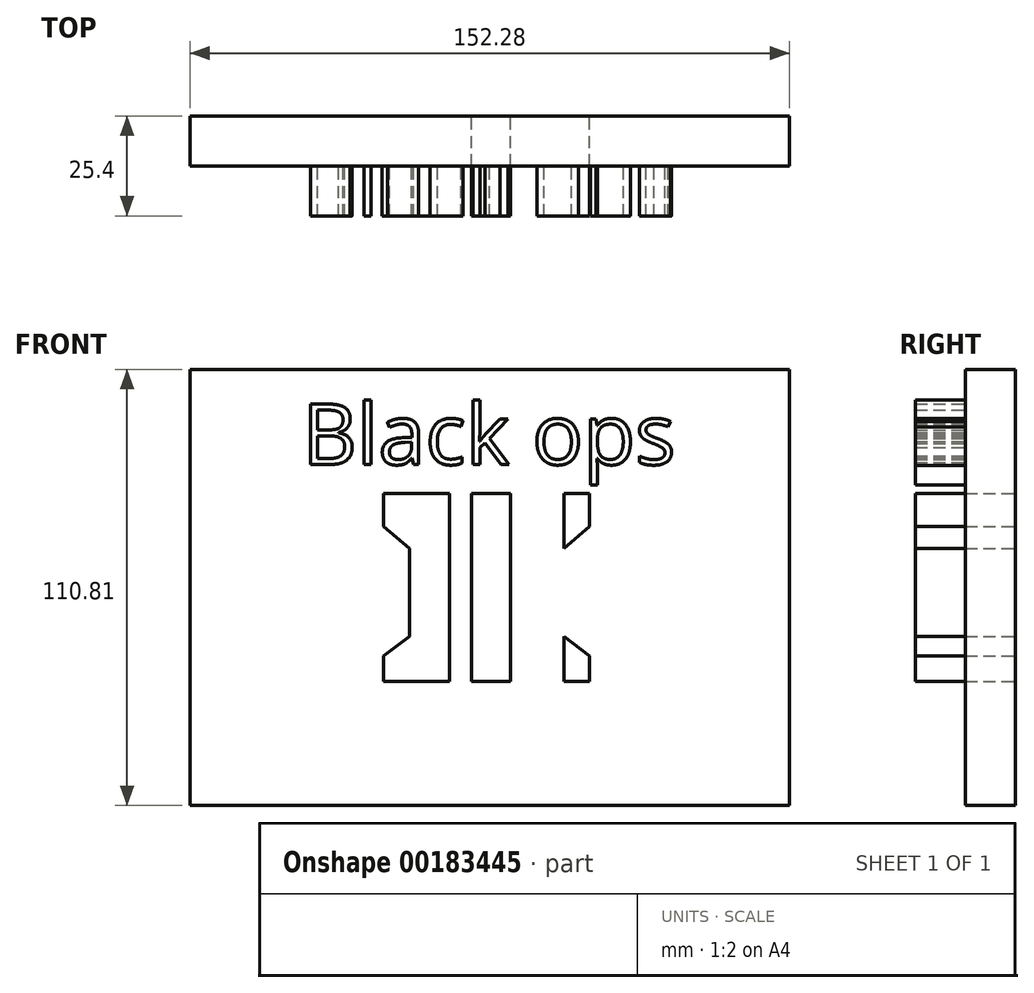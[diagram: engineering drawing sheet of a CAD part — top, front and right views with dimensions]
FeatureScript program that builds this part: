
annotation { "Feature Type Name" : "Feature", "Feature Type Description" : "" }
export const myFeature = defineFeature(function(context is Context, id is Id, definition is map)
    precondition{}
    {
        {
            var Q0;
            Q0=qCreatedBy(makeId("Front.planeOp"),FACE);
            var sketch = newSketch(context, id + "F0", { "sketchPlane" : qUnion([Q0])});
            skLineSegment(sketch, "E0.bottom", {"start": v(-4.33, 24.3) * mm, "end": v(5.57, 24.3) * mm});
            skLineSegment(sketch, "E0.top", {"start": v(-4.33, -23.37) * mm, "end": v(5.57, -23.37) * mm});
            skLineSegment(sketch, "E0.left", {"start": v(-4.33, 24.3) * mm, "end": v(-4.33, -23.37) * mm});
            skLineSegment(sketch, "E0.right", {"start": v(5.57, 24.3) * mm, "end": v(5.57, -23.37) * mm});
            skLineSegment(sketch, "E1.bottom", {"start": v(9.6, 24.3) * mm, "end": v(19.2, 24.3) * mm});
            skLineSegment(sketch, "E1.top", {"start": v(9.6, 24.3) * mm, "end": v(19.2, 24.3) * mm});
            skLineSegment(sketch, "E1.left", {"start": v(9.6, 24.3) * mm, "end": v(9.6, 24.3) * mm});
            skLineSegment(sketch, "E1.right", {"start": v(19.2, 24.3) * mm, "end": v(19.2, 24.3) * mm});
            skLineSegment(sketch, "E2.bottom", {"start": v(19.2, 24.3) * mm, "end": v(10.21, 24.3) * mm});
            skLineSegment(sketch, "E2.top", {"start": v(19.2, -23.37) * mm, "end": v(10.21, -23.37) * mm});
            skLineSegment(sketch, "E2.left", {"start": v(19.2, 24.3) * mm, "end": v(19.2, -23.37) * mm});
            skLineSegment(sketch, "E2.right", {"start": v(10.21, 24.3) * mm, "end": v(10.21, -23.37) * mm});
            skLineSegment(sketch, "E3.bottom", {"start": v(-10.52, 24.3) * mm, "end": v(-20.12, 24.3) * mm});
            skLineSegment(sketch, "E3.top", {"start": v(-10.52, 24.3) * mm, "end": v(-20.12, 24.3) * mm});
            skLineSegment(sketch, "E3.left", {"start": v(-10.52, 24.3) * mm, "end": v(-10.52, 24.3) * mm});
            skLineSegment(sketch, "E3.right", {"start": v(-20.12, 24.3) * mm, "end": v(-20.12, 24.3) * mm});
            skLineSegment(sketch, "E4.bottom", {"start": v(-20.12, 24.3) * mm, "end": v(-9.9, 24.3) * mm});
            skLineSegment(sketch, "E4.top", {"start": v(-20.12, -23.37) * mm, "end": v(-9.9, -23.37) * mm});
            skLineSegment(sketch, "E4.left", {"start": v(-20.12, 24.3) * mm, "end": v(-20.12, -23.37) * mm});
            skLineSegment(sketch, "E4.right", {"start": v(-9.9, 24.3) * mm, "end": v(-9.9, -23.37) * mm});
            skLineSegment(sketch, "E5", {"start": v(-20.12, 24.3) * mm, "end": v(-26.62, 24.3) * mm});
            skLineSegment(sketch, "E6", {"start": v(-26.62, 24.3) * mm, "end": v(-26.62, 15.94) * mm});
            skLineSegment(sketch, "E7", {"start": v(-26.62, 15.94) * mm, "end": v(-20.12, 10.37) * mm});
            skLineSegment(sketch, "E8", {"start": v(-20.12, 10.37) * mm, "end": v(-20.12, -23.37) * mm});
            skLineSegment(sketch, "E9", {"start": v(-20.12, -23.37) * mm, "end": v(-26.62, -23.37) * mm});
            skLineSegment(sketch, "E10", {"start": v(-26.62, -23.37) * mm, "end": v(-26.62, -16.87) * mm});
            skLineSegment(sketch, "E11", {"start": v(-26.62, -16.87) * mm, "end": v(-20.12, -11.92) * mm});
            skLineSegment(sketch, "E12", {"start": v(19.2, 24.3) * mm, "end": v(25.69, 24.3) * mm});
            skLineSegment(sketch, "E13", {"start": v(25.69, 24.3) * mm, "end": v(25.69, 15.94) * mm});
            skLineSegment(sketch, "E14", {"start": v(25.69, 15.94) * mm, "end": v(19.2, 10.37) * mm});
            skLineSegment(sketch, "E15", {"start": v(19.2, -23.37) * mm, "end": v(25.69, -23.37) * mm});
            skLineSegment(sketch, "E16", {"start": v(25.69, -23.37) * mm, "end": v(25.69, -16.87) * mm});
            skLineSegment(sketch, "E17", {"start": v(25.69, -16.87) * mm, "end": v(19.2, -11.92) * mm});
            skSolve(sketch);
        }
        {
            var Q0;
            Q0=qCreatedBy(makeId("Front.planeOp"),FACE);
            var sketch = newSketch(context, id + "F1", { "sketchPlane" : qUnion([Q0])});
            skSolve(sketch);
        }
        {
            var Q0;
            Q0 = qSketchRegion(id + "F1", true);
            var Q1;
            {var subQ0=sQuery(id+"F0.wireOp",EDGE,"E9");Q1=makeQuery(id+"F0.imprint","IMPRINT",FACE,{"disambiguationData":[TD([[makeQuery(id+"F0.imprint","IMPRINT",EDGE,{"derivedFrom":subQ0}),-1.0]])]});}
            var Q2;
            {var subQ4=sQuery(id+"F0.wireOp",EDGE,"E4.top");Q2=makeQuery(id+"F0.imprint","IMPRINT",FACE,{"disambiguationData":[TD([[makeQuery(id+"F0.imprint","IMPRINT",EDGE,{"derivedFrom":subQ4}),1.0]])]});}
            var Q3;
            Q3=makeQuery(id+"F0.imprint","IMPRINT",FACE,{"disambiguationData":[TD([[makeQuery(id+"F0.imprint","IMPRINT",EDGE,{"derivedFrom":sQuery(id+"F0.wireOp",EDGE,"E4.left")}),-1.0]])]});
            var Q4;
            Q4=makeQuery(id+"F0.imprint","IMPRINT",FACE,{"disambiguationData":[TD([[makeQuery(id+"F0.imprint","IMPRINT",EDGE,{"derivedFrom":sQuery(id+"F0.wireOp",EDGE,"E0.bottom")}),-1.0]])]});
            var Q5;
            {var subQ3=sQuery(id+"F0.wireOp",EDGE,"E2.bottom");Q5=makeQuery(id+"F0.imprint","IMPRINT",FACE,{"disambiguationData":[TD([[makeQuery(id+"F0.imprint","IMPRINT",EDGE,{"derivedFrom":subQ3}),1.0]])]});}
            var Q6;
            {var subQ0=sQuery(id+"F0.wireOp",EDGE,"E12");Q6=makeQuery(id+"F0.imprint","IMPRINT",FACE,{"disambiguationData":[TD([[makeQuery(id+"F0.imprint","IMPRINT",EDGE,{"derivedFrom":subQ0}),-1.0]])]});}
            var Q7;
            {var subQ0=sQuery(id+"F0.wireOp",EDGE,"E15");Q7=makeQuery(id+"F0.imprint","IMPRINT",FACE,{"disambiguationData":[TD([[makeQuery(id+"F0.imprint","IMPRINT",EDGE,{"derivedFrom":subQ0}),1.0]])]});}
            extrude(context, id + "F2", {"entities" : qUnion([Q0, Q1, Q2, Q3, Q4, Q5, Q6, Q7]), "depth" : 25.4 * mm});
        }
        {
            var Q0;
            Q0=qCreatedBy(makeId("Front.planeOp"),FACE);
            var sketch = newSketch(context, id + "F3", { "sketchPlane" : qUnion([Q0])});
            skLineSegment(sketch, "E18.bottom", {"start": v(76.45, 55.87) * mm, "end": v(-75.83, 55.87) * mm});
            skLineSegment(sketch, "E18.top", {"start": v(76.45, -54.94) * mm, "end": v(-75.83, -54.94) * mm});
            skLineSegment(sketch, "E18.left", {"start": v(76.45, 55.87) * mm, "end": v(76.45, -54.94) * mm});
            skLineSegment(sketch, "E18.right", {"start": v(-75.83, 55.87) * mm, "end": v(-75.83, -54.94) * mm});
            skSolve(sketch);
        }
        {
            var Q0;
            Q0=makeQuery(id+"F3.imprint","IMPRINT",FACE,{"disambiguationData":[TD([[makeQuery(id+"F3.imprint","IMPRINT",EDGE,{"derivedFrom":sQuery(id+"F3.wireOp",EDGE,"E18.bottom")}),1.0]])]});
            extrude(context, id + "F4", {"entities" : qUnion([Q0]), "depth" : 12.7 * mm});
        }
        {
            var Q0;
            Q0=qCreatedBy(makeId("Front.planeOp"),FACE);
            var sketch = newSketch(context, id + "F5", { "sketchPlane" : qUnion([Q0])});
            skText(sketch, "E19", { "text": "Black ops ", "fontName": "OpenSans-Regular.ttf"});
            const initialGuessF5  = {"E19": [-0.04736, 0.03173, 1, 0, 0.01548]};
            skSetInitialGuess(sketch, initialGuessF5);
            skSolve(sketch);
        }
        {
            var Q0;
            Q0 = qSketchRegion(id + "F5", true);
            extrude(context, id + "F6", {"entities" : qUnion([Q0]), "operationType" : NewBodyOperationType.ADD, "depth" : 25.4 * mm});
        }
    });
